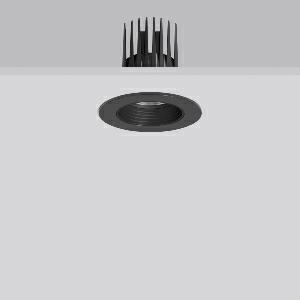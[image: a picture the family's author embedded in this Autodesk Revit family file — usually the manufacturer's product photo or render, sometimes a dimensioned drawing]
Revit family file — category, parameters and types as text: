
# Revit family: heledon_mini_e_901751_003_2_1097
name_source: partatom
category: Lighting Fixtures
units: mm (PartAtom-declared; Revit-internal decimal feet)

## family parameters
Cut with Voids When Loaded = No
Host = Face
Light Source = No
Part Type = Normal
Room Calculation Point = No
Round Connector Dimension = Use Diameter
Shared = No

## types (1)
- HELEDON mini E (1 x LED Modul 927, 3000 lm, 2700)
    Apparent Load = 29 VA
    Approval mark = CE
    CIE Flux Codes = 99 100 100 100 100
    Color Rendering = 92
    Color Temperature = 2700
    Default Elevation = 1800 mm
    Description = Series: HELEDON mini
Round recessed downlight. Housing: die-cast aluminium, powder-coated. Black plastic ring and recessed LED to prevent glare from the side. Optical assembly with lens made of plastic (polycarbonate) for the best homogeneous light distribution - can be changed without tools. Best colour rendering index Ra>90. Suitable for Recessed ceiling mounting. Installation without tools thanks to spring fastening system. Including separate LED converter with connecting cable 600 mm.High quality converter without flickering and stroboscopic effect. Through-wiring box (5 pole) available as accessory. The following accessories can be mounted without use of tools: interchangeable lenses, decorative glasses, honeycomb louvre, clear and frosted diffusers, white interchangeable plastic ring. 
Colour: deep black, matt (RAL 9005)
Diameter: 124 mm
Height: 3 mm
Cut-out diameter: 114 mm
Recess height: 170 mm
Luminaire: recess height: 120 mm
Lamp: LED
Socket: without socket
Colour temperature: 2700K
Colour rendering index (CRI): 92
System power: 29 W
Rated luminous flux: 3000 lm
Luminous efficiency: 103 lm/W
Control gear: Regulated power supply
Protection class: II
Type of protection: IP 20
    Height = 0 mm  [stored 0 ft]
    Lamp = 1 x LED Modul 927
    Lamp Light Flux = 3000 lm
    Lamp count = 1
    Length = 124 mm  [stored 0.406824 ft]
    Lifetime = 50000 h
    Luminous efficacy = 103 lm/W
    Manufacturer = RZB
    ModVariant = No
    Model = 901751.003.2
    Mounting Place = Ceiling
    Mounting Type = Recessed
    Number of Poles = 1
    OnlyDefault = Yes
    Power Factor = 1
    Product Name = HELEDON mini E
    Product group = Recessed downlights
    ProductGroupID = 402
    Protection Class = Protection class II
    Protection Degree = IP 20
    RLX_Detail_Level = 1
    RLX_Emergency_Light_Flux = 0 lm
    RLX_Emergency_Type = 0
    RLX_Emergency_Type_DB = No
    RlxData = <blob elided: 127593 chars, md5=b52d1b0b>
    Socket = socket
    Standby Power = 0 W
    System Light Flux = 3000 lm
    System Power = 29 W
    Type Comments = Product without accessories
    Type Image = 901656.003.jpg
    URL = http://relux.com
    VarID = ---
    Voltage = 230 V
    Voltage Range = 220-240 V
    Weight = 0.00 kg
    Width = 0 mm  [stored 0 ft]

note: [stored X ft] marks values corroborated as IEEE doubles in the binary element streams (Revit-internal decimal feet)

## geometry (parser evidence)
native form markers: Blend x4, Sweep x10
no freeform markers — native parametric forms only
